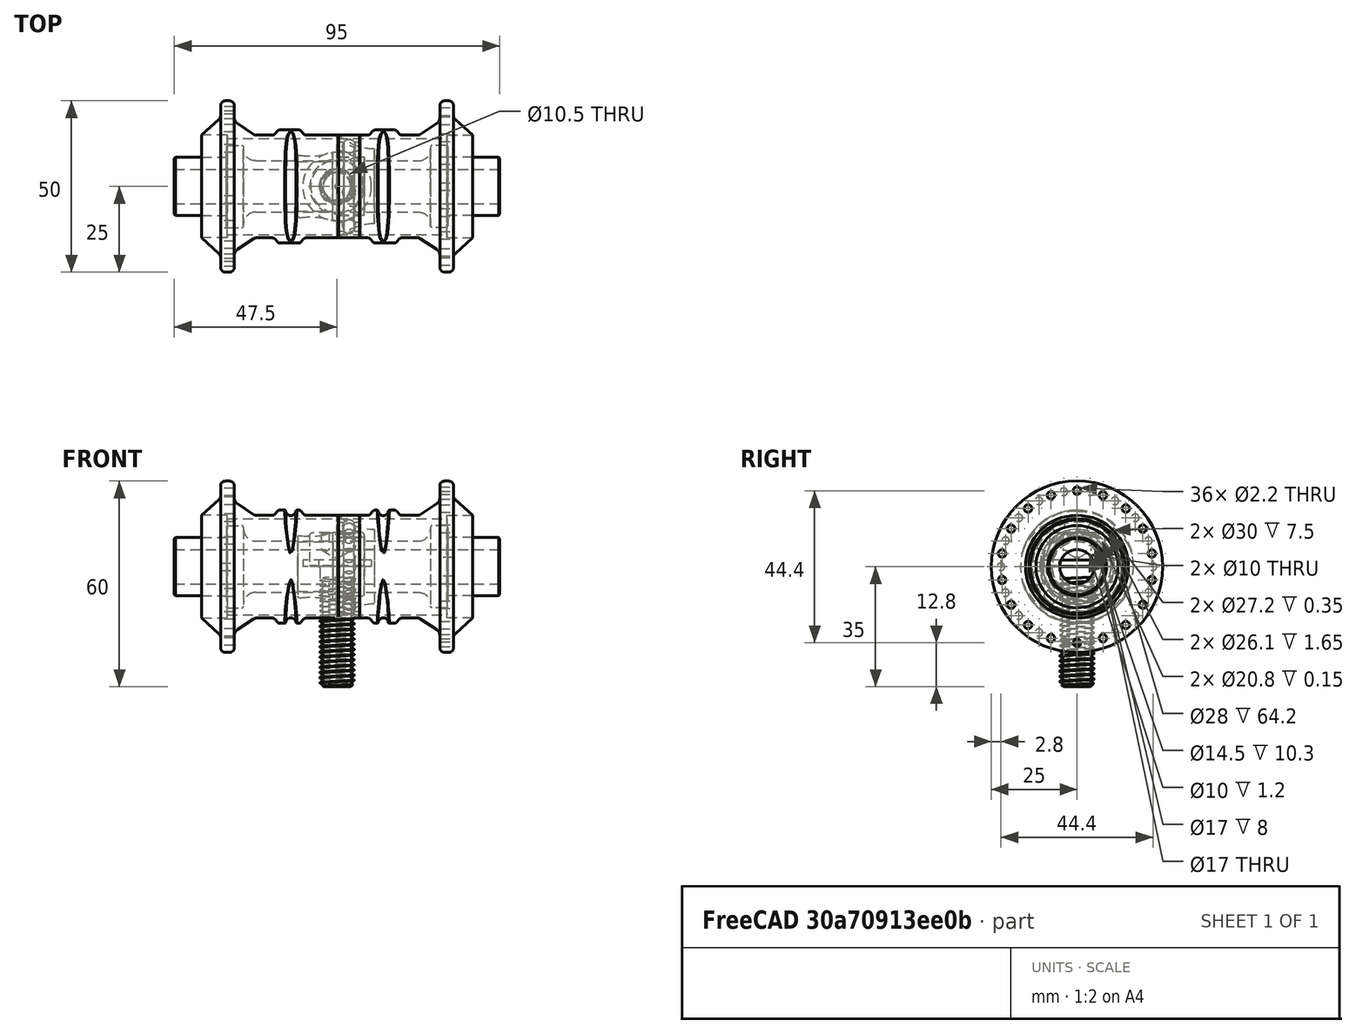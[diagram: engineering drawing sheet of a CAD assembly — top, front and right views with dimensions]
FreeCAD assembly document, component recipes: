
FREECAD ASSEMBLY — COMPONENT RECIPES ("Bike Hub")

This assembly document has 12 components, labeled P0..P11 below (a component is one placed body or linked part). 6 of them carry a construction recipe — the FreeCAD feature program that regenerates the part from scratch, quoted from this document or its linked companion documents; the rest are supplied as boundary geometry only. No exploded tour is included for this assembly.
COMPONENT P0 — recipe-attached ("Axle001", modeled in this document).
Construction recipe (the document's own serialized feature program — sketch geometry with constraints, then the solid features built on it; lengths are millimeters unless a unit is written):

FEATURE [Sketcher::SketchObject] Sketch
  ArcFitTolerance = 1e-06
  AttachmentSupport = -> [XZ_Plane]
  FullyConstrained = true
  MakeInternals = false
  MapMode = 5
  Placement = pos=(0,0,0) rot=(1,0,0;1.5708rad)
  sketch-geometry (19):
    g0: LineSegment StartX=0 StartY=0 StartZ=0 EndX=-47.5 EndY=0 EndZ=0
    g1: LineSegment StartX=-47.5 StartY=0 StartZ=0 EndX=-47.5 EndY=8.14645 EndZ=0
    g2: LineSegment StartX=-47.1464 StartY=8.5 StartZ=0 EndX=-32.8 EndY=8.5 EndZ=0
    g3: LineSegment StartX=-32.3 StartY=9 StartZ=0 EndX=-32.3 EndY=11.5 EndZ=0
    g4: LineSegment StartX=-31.8 StartY=12 StartZ=0 EndX=-27.8 EndY=12 EndZ=0
    g5: LineSegment StartX=-27.3 StartY=11.5 StartZ=0 EndX=-27.3 EndY=11 EndZ=0
    g6: LineSegment StartX=-23.8 StartY=7.5 StartZ=0 EndX=0 EndY=7.5 EndZ=0
    g7: LineSegment StartX=0 StartY=7.5 StartZ=0 EndX=0 EndY=0 EndZ=0
    g8: ArcOfCircle CenterX=-27.8 CenterY=11.5 CenterZ=0 NormalX=0 NormalY=0 NormalZ=1 AngleXU=0 Radius=0.5 StartAngle=0 EndAngle=1.5708
    g9: GeomPoint [constr] X=-27.3 Y=12 Z=0
    g10: ArcOfCircle CenterX=-23.8 CenterY=11 CenterZ=0 NormalX=0 NormalY=0 NormalZ=1 AngleXU=0 Radius=3.5 StartAngle=3.14159 EndAngle=4.71239
    g11: GeomPoint [constr] X=-27.3 Y=7.5 Z=0
    g12: ArcOfCircle CenterX=-31.8 CenterY=11.5 CenterZ=0 NormalX=0 NormalY=0 NormalZ=1 AngleXU=0 Radius=0.5 StartAngle=1.5708 EndAngle=3.14159
    g13: GeomPoint [constr] X=-32.3 Y=12 Z=0
    g14: ArcOfCircle CenterX=-32.8 CenterY=9 CenterZ=0 NormalX=0 NormalY=0 NormalZ=1 AngleXU=0 Radius=0.5 StartAngle=4.71239 EndAngle=6.28319
    g15: GeomPoint [constr] X=-32.3 Y=8.5 Z=0
    g16: ArcOfCircle [constr] CenterX=-47.1464 CenterY=8.14645 CenterZ=0 NormalX=0 NormalY=0 NormalZ=1 AngleXU=0 Radius=0.353553 StartAngle=1.5708 EndAngle=3.14159
    g17: GeomPoint [constr] X=-47.5 Y=8.5 Z=0
    g18: LineSegment StartX=-47.1464 StartY=8.5 StartZ=0 EndX=-47.5 EndY=8.14645 EndZ=0
  constraints (45):
    c: Coincident(g-1,g0)
    c: PointOnObject(g0,g-1)
    c: Coincident(g0,g1)
    c: Vertical(g1)
    c: Horizontal(g2)
    c: Horizontal(g4)
    c: Vertical(g5)
    c: Horizontal(g6)
    c: Coincident(g6,g7)
    c: Coincident(g7,g0)
    c: Vertical(g7)
    c: Vertical(g3)
    c: DistanceX(g0,g0) = 47.5
    c: DistanceY(g1,g17) = 8.5
    c: Distance(g13,g0) = 12
    c: DistanceX(g13,g-1) = 32.3
    c: DistanceX(g13,g9) = 5
    c: DistanceY(g7,g7) = 7.5
    c: PointOnObject(g9,g4)
    c: PointOnObject(g9,g5)
    c: Tangent(g4,g8) = 1.5708
    c: Tangent(g5,g8) = 1.5708
    c: PointOnObject(g11,g5)
    c: PointOnObject(g11,g6)
    c: Tangent(g5,g10) = -1.5708
    c: Tangent(g6,g10) = -1.5708
    c: PointOnObject(g13,g3)
    c: PointOnObject(g13,g4)
    c: Tangent(g3,g12) = 1.5708
    c: Tangent(g4,g12) = 1.5708
    c: PointOnObject(g15,g2)
    c: PointOnObject(g15,g3)
    c: Tangent(g2,g14) = -1.5708
    c: Tangent(g3,g14) = -1.5708
    c: Radius(g8) = 0.5
    c: Equal(g8,g12)
    c: Equal(g12,g14)
    c: Radius(g10) = 3.5
    c: PointOnObject(g17,g1)
    c: PointOnObject(g17,g2)
    c: Tangent(g1,g16) = 1.5708
    c: Tangent(g2,g16) = 1.5708
    c: Coincident(g18,g1)
    c: Coincident(g18,g2)
    c: Distance(g18,g18) = 0.5
FEATURE [PartDesign::Revolution] Revolution
  Angle = 360
  Angle2 = 60
  Axis = (1,0,0)
  Base = (0,0,0)
  Placement = pos=(0,0,0) rot=(1,0,0;1.5708rad)
  Profile = -> Sketch
  ReferenceAxis = -> X_Axis
  Refine = true
  Suppressed = false
  Type = 0
FEATURE [PartDesign::Hole] Hole
  BaseFeature = -> Revolution
  CustomThreadClearance = 0
  Depth = 117.922
  DepthType = 1
  Diameter = 10
  DrillForDepth = false
  DrillPoint = 1
  DrillPointAngle = 118
  HoleCutCountersinkAngle = 90
  HoleCutCustomValues = false
  HoleCutDepth = 0
  HoleCutDiameter = 6.1
  HoleCutType = 0
  ModelThread = false
  Placement = pos=(0,0,0) rot=(1,0,0;1.5708rad)
  Profile = -> Revolution [Face5]
  Refine = true
  Suppressed = false
  Tapered = false
  TaperedAngle = 90
  ThreadClass = 0
  ThreadDepth = 117.922
  ThreadDepthType = 0
  ThreadDirection = 0
  ThreadFit = 0
  ThreadSize = 0
  ThreadType = 0
  Threaded = false
  UseCustomThreadClearance = false
FEATURE [PartDesign::Mirrored] Mirrored
  BaseFeature = -> Hole
  MirrorPlane = -> YZ_Plane
  Originals = -> [Hole]
  Placement = pos=(0,0,0) rot=(1,0,0;1.5708rad)
  Refine = true
  Suppressed = false
  TransformMode = 1
FEATURE [PartDesign::Body] Body  label="Axle"
  AllowCompound = false
  Group = -> [Sketch,Revolution,Hole,Mirrored]
  Origin = -> Origin
  Tip = -> Mirrored
COMPONENT P1 — geometry summary ("Bearing001"; no construction recipe available for this part):
  bounding box: 30.0 x 30.0 x 7.0 mm
  tessellated surface: 109,814 triangles
  volume: 2172 mm^3 (34% of its bounding box)
  symmetry: mirror-symmetric across its x mid-plane
COMPONENT P2 — geometry summary ("Bearing002"; no construction recipe available for this part):
  bounding box: 30.0 x 30.0 x 7.0 mm
  tessellated surface: 109,814 triangles
  volume: 2172 mm^3 (34% of its bounding box)
  symmetry: mirror-symmetric across its x mid-plane
COMPONENT P3 — recipe-attached ("Bearing Cover001", modeled in this document).
Construction recipe (the document's own serialized feature program — sketch geometry with constraints, then the solid features built on it; lengths are millimeters unless a unit is written):

FEATURE [Sketcher::SketchObject] Sketch008
  ArcFitTolerance = 1e-06
  AttachmentSupport = -> [XZ_Plane002]
  FullyConstrained = true
  MakeInternals = false
  MapMode = 5
  Placement = pos=(0,0,0) rot=(1,0,0;1.5708rad)
  sketch-geometry (8):
    g0: LineSegment StartX=0 StartY=0 StartZ=0 EndX=10.9 EndY=0 EndZ=0
    g1: LineSegment StartX=0 StartY=0 StartZ=0 EndX=0 EndY=10.9 EndZ=0
    g2: LineSegment StartX=0 StartY=10.9 StartZ=0 EndX=0.3 EndY=10.9 EndZ=0
    g3: LineSegment StartX=0.3 StartY=10.9 StartZ=0 EndX=0.3 EndY=15 EndZ=0
    g4: LineSegment StartX=0.3 StartY=15 StartZ=0 EndX=0.5 EndY=15 EndZ=0
    g5: LineSegment StartX=10.9 StartY=0 StartZ=0 EndX=10.9 EndY=10.9 EndZ=0
    g6: ArcOfCircle CenterX=10.9 CenterY=26.1402 CenterZ=0 NormalX=0 NormalY=0 NormalZ=1 AngleXU=0 Radius=15.2402 StartAngle=3.96134 EndAngle=4.71239
    g7: LineSegment [constr] StartX=10.9 StartY=10.9 StartZ=0 EndX=20.01 EndY=10.9 EndZ=0
  constraints (24):
    c: Coincident(g-1,g0)
    c: PointOnObject(g0,g-1)
    c: Coincident(g0,g1)
    c: PointOnObject(g1,g-2)
    c: Coincident(g1,g2)
    c: Horizontal(g2)
    c: Coincident(g2,g3)
    c: DistanceX(g0,g0) = 10.9
    c: DistanceY(g1,g1) = 10.9
    c: Coincident(g4,g3)
    c: Vertical(g3)
    c: Horizontal(g4)
    c: DistanceX(g2,g2) = 0.3
    c: DistanceX(g4,g4) = 0.2
    c: DistanceY(g-1,g3) = 15
    c: Coincident(g0,g5)
    c: Vertical(g5)
    c: Coincident(g6,g5)
    c: Coincident(g6,g4)
    c: Coincident(g7,g5)
    c: Horizontal(g7)
    c: Tangent(g6,g7)
    c: Horizontal(g5,g2)
    c: DistanceX(g7,g7) = 9.11
FEATURE [PartDesign::Revolution] Revolution002
  Angle = 360
  Angle2 = 60
  Axis = (1,0,0)
  Base = (0,0,0)
  Placement = pos=(0,0,0) rot=(1,0,0;1.5708rad)
  Profile = -> Sketch008
  ReferenceAxis = -> X_Axis002
  Refine = true
  Suppressed = false
  Type = 0
FEATURE [Sketcher::SketchObject] Sketch009
  ArcFitTolerance = 1e-06
  AttachmentSupport = -> [Revolution002]
  FullyConstrained = true
  MakeInternals = false
  MapMode = 5
  Placement = pos=(0,0,0) rot=(0.707107,0,-0.707107;3.14159rad)
  sketch-geometry (1):
    g0: Circle CenterX=0 CenterY=0 CenterZ=0 NormalX=0 NormalY=0 NormalZ=1 AngleXU=0 Radius=8.5
  constraints (2):
    c: Coincident(g0,g-1)
    c: Diameter(g0) = 17
FEATURE [PartDesign::Pocket] Pocket004
  BaseFeature = -> Revolution002
  Direction = (1,0,2e-16)
  Length = 8
  Length2 = 5
  Placement = pos=(0,0,0) rot=(1,0,0;1.5708rad)
  Profile = -> Sketch009
  ReferenceAxis = -> Sketch009 [N_Axis]
  Refine = true
  Suppressed = false
  Type = 0
FEATURE [Sketcher::SketchObject] Sketch010
  ArcFitTolerance = 1e-06
  AttachmentSupport = -> [Pocket004]
  FullyConstrained = true
  MakeInternals = false
  MapMode = 5
  Placement = pos=(10.9,0,0) rot=(0.707107,0,0.707107;3.14159rad)
  sketch-geometry (1):
    g0: Circle CenterX=0 CenterY=0 CenterZ=0 NormalX=0 NormalY=0 NormalZ=1 AngleXU=0 Radius=5
  constraints (2):
    c: Coincident(g0,g-1)
    c: Diameter(g0) = 10
FEATURE [PartDesign::Pocket] Pocket005
  BaseFeature = -> Pocket004
  Direction = (-1,0,2e-16)
  Length = 5
  Length2 = 5
  Placement = pos=(0,0,0) rot=(1,0,0;1.5708rad)
  Profile = -> Sketch010
  ReferenceAxis = -> Sketch010 [N_Axis]
  Refine = true
  Suppressed = false
  Type = 1
FEATURE [PartDesign::Body] Body002  label="Bearing Cover"
  AllowCompound = false
  Group = -> [Sketch008,Revolution002,Sketch009,Pocket004,Sketch010,Pocket005]
  Origin = -> Origin002
  Tip = -> Pocket005
COMPONENT P4 — same part as P3; its construction recipe is shown at P3.
COMPONENT P5 — recipe-attached ("Bolt Cover001", modeled in this document).
Construction recipe (the document's own serialized feature program — sketch geometry with constraints, then the solid features built on it; lengths are millimeters unless a unit is written):

FEATURE [Sketcher::SketchObject] Sketch011
  ArcFitTolerance = 1e-06
  AttachmentSupport = -> [XZ_Plane004]
  FullyConstrained = true
  MakeInternals = false
  MapMode = 5
  Placement = pos=(0,0,0) rot=(1,0,0;1.5708rad)
  sketch-geometry (5):
    g0: LineSegment StartX=0 StartY=0 StartZ=0 EndX=-11.5 EndY=0 EndZ=0
    g1: LineSegment StartX=-11.5 StartY=0 StartZ=0 EndX=-11.5 EndY=9.2 EndZ=0
    g2: LineSegment StartX=0 StartY=0 StartZ=0 EndX=0 EndY=10 EndZ=0
    g3: LineSegment StartX=0 StartY=10 StartZ=0 EndX=-1.3 EndY=10 EndZ=0
    g4: ArcOfCircle CenterX=-7.9118 CenterY=28.8755 CenterZ=0 NormalX=0 NormalY=0 NormalZ=1 AngleXU=0 Radius=20 StartAngle=4.532 EndAngle=5.04932
  constraints (15):
    c: Coincident(g-1,g0)
    c: PointOnObject(g0,g-1)
    c: Coincident(g0,g1)
    c: Vertical(g1)
    c: Coincident(g0,g2)
    c: PointOnObject(g2,g-2)
    c: Coincident(g2,g3)
    c: Horizontal(g3)
    c: Coincident(g4,g3)
    c: Coincident(g4,g1)
    c: DistanceX(g0,g0) = 11.5
    c: DistanceY(g1,g1) = 9.2
    c: DistanceY(g2,g2) = 10
    c: DistanceX(g3,g3) = 1.3
    c: Radius(g4) = 20
FEATURE [PartDesign::Revolution] Revolution003
  Angle = 360
  Angle2 = 60
  Axis = (1,0,0)
  Base = (0,0,0)
  Placement = pos=(0,0,0) rot=(1,0,0;1.5708rad)
  Profile = -> Sketch011
  ReferenceAxis = -> X_Axis004
  Refine = true
  Suppressed = false
  Type = 0
FEATURE [Sketcher::SketchObject] Sketch012
  ArcFitTolerance = 1e-06
  AttachmentSupport = -> [Revolution003]
  FullyConstrained = true
  MakeInternals = false
  MapMode = 5
  Placement = pos=(-11.5,0,0) rot=(0.707107,0,-0.707107;3.14159rad)
  sketch-geometry (1):
    g0: Circle CenterX=0 CenterY=0 CenterZ=0 NormalX=0 NormalY=0 NormalZ=1 AngleXU=0 Radius=5
  constraints (2):
    c: Diameter(g0) = 10
    c: Coincident(g0,g-1)
FEATURE [PartDesign::Hole] Hole001
  BaseFeature = -> Revolution003
  CustomThreadClearance = 0
  Depth = 61.6685
  DepthType = 1
  Diameter = 10
  DrillForDepth = false
  DrillPoint = 1
  DrillPointAngle = 118
  HoleCutCountersinkAngle = 90
  HoleCutCustomValues = false
  HoleCutDepth = 10.3
  HoleCutDiameter = 14.5
  HoleCutType = 1
  ModelThread = false
  Placement = pos=(0,0,0) rot=(1,0,0;1.5708rad)
  Profile = -> Sketch012
  Refine = true
  Suppressed = false
  Tapered = false
  TaperedAngle = 90
  ThreadClass = 0
  ThreadDepth = 61.6685
  ThreadDepthType = 0
  ThreadDirection = 0
  ThreadFit = 0
  ThreadSize = 0
  ThreadType = 0
  Threaded = false
  UseCustomThreadClearance = false
FEATURE [PartDesign::Fillet] Fillet001
  Base = -> Hole001 [Edge1]
  BaseFeature = -> Hole001
  Placement = pos=(0,0,0) rot=(1,0,0;1.5708rad)
  Radius = 0.5
  Refine = true
  SupportTransform = false
  Suppressed = false
  UseAllEdges = false
FEATURE [PartDesign::Body] Body003  label="Bolt Cover"
  AllowCompound = false
  Group = -> [Sketch011,Revolution003,Sketch012,Hole001,Fillet001]
  Origin = -> Origin004
  Tip = -> Fillet001
COMPONENT P6 — same part as P5; its construction recipe is shown at P5.
COMPONENT P7 — recipe-attached ("Hub Cage001", modeled in this document).
Construction recipe (the document's own serialized feature program — sketch geometry with constraints, then the solid features built on it; lengths are millimeters unless a unit is written):

FEATURE [Sketcher::SketchObject] Sketch001
  ArcFitTolerance = 1e-06
  AttachmentSupport = -> [XZ_Plane001]
  FullyConstrained = true
  MakeInternals = false
  MapMode = 5
  Placement = pos=(0,0,0) rot=(1,0,0;1.5708rad)
  sketch-geometry (31):
    g0: LineSegment StartX=0 StartY=0 StartZ=0 EndX=-39.6 EndY=0 EndZ=0
    g1: LineSegment StartX=-39.6 StartY=0 StartZ=0 EndX=-39.6 EndY=15 EndZ=0
    g2: LineSegment StartX=-39.6 StartY=15 StartZ=0 EndX=-34.4676 EndY=19.5825 EndZ=0
    g3: LineSegment StartX=-34 StartY=20.6268 StartZ=0 EndX=-34 EndY=23.6 EndZ=0
    g4: LineSegment StartX=-32.6 StartY=25 StartZ=0 EndX=-31.4 EndY=25 EndZ=0
    g5: LineSegment StartX=-30 StartY=23.6 StartZ=0 EndX=-30 EndY=20.0704 EndZ=0
    g6: LineSegment StartX=-29.1094 StartY=18.4063 StartZ=0 EndX=-24.2519 EndY=15.1679 EndZ=0
    g7: LineSegment StartX=-23.6972 StartY=15 StartZ=0 EndX=-18.8806 EndY=15 EndZ=0
    g8: LineSegment StartX=-18.0998 StartY=15.3753 StartZ=0 EndX=-17.5002 EndY=16.1247 EndZ=0
    g9: LineSegment StartX=-16.7194 StartY=16.5 StartZ=0 EndX=-11.1806 EndY=16.5 EndZ=0
    g10: LineSegment StartX=-10.3998 StartY=16.1247 StartZ=0 EndX=-9.80024 EndY=15.3753 EndZ=0
    g11: LineSegment StartX=-9.01938 StartY=15 StartZ=0 EndX=0 EndY=15 EndZ=0
    g12: LineSegment StartX=0 StartY=15 StartZ=0 EndX=0 EndY=0 EndZ=0
    g13: ArcOfCircle CenterX=-32.6 CenterY=23.6 CenterZ=0 NormalX=0 NormalY=0 NormalZ=1 AngleXU=0 Radius=1.4 StartAngle=1.5708 EndAngle=3.14159
    g14: GeomPoint [constr] X=-34 Y=25 Z=0
    g15: ArcOfCircle CenterX=-31.4 CenterY=23.6 CenterZ=0 NormalX=0 NormalY=0 NormalZ=1 AngleXU=0 Radius=1.4 StartAngle=0 EndAngle=1.5708
    g16: GeomPoint [constr] X=-30 Y=25 Z=0
    g17: ArcOfCircle CenterX=-35.4 CenterY=20.6268 CenterZ=0 NormalX=0 NormalY=0 NormalZ=1 AngleXU=0 Radius=1.4 StartAngle=5.44124 EndAngle=6.28319
    g18: GeomPoint [constr] X=-34 Y=20 Z=0
    g19: ArcOfCircle CenterX=-28 CenterY=20.0704 CenterZ=0 NormalX=0 NormalY=0 NormalZ=1 AngleXU=0 Radius=2 StartAngle=3.14159 EndAngle=4.12439
    g20: GeomPoint [constr] X=-30 Y=19 Z=0
    g21: ArcOfCircle CenterX=-23.6972 CenterY=16 CenterZ=0 NormalX=0 NormalY=0 NormalZ=1 AngleXU=0 Radius=1 StartAngle=4.12439 EndAngle=4.71239
    g22: GeomPoint [constr] X=-24 Y=15 Z=0
    g23: ArcOfCircle CenterX=-18.8806 CenterY=16 CenterZ=0 NormalX=0 NormalY=0 NormalZ=1 AngleXU=0 Radius=1 StartAngle=4.71239 EndAngle=5.60844
    g24: GeomPoint [constr] X=-18.4 Y=15 Z=0
    g25: ArcOfCircle CenterX=-16.7194 CenterY=15.5 CenterZ=0 NormalX=0 NormalY=0 NormalZ=1 AngleXU=0 Radius=1 StartAngle=1.5708 EndAngle=2.46685
    g26: GeomPoint [constr] X=-17.2 Y=16.5 Z=0
    g27: ArcOfCircle CenterX=-11.1806 CenterY=15.5 CenterZ=0 NormalX=0 NormalY=0 NormalZ=1 AngleXU=0 Radius=1 StartAngle=0.674741 EndAngle=1.5708
    g28: GeomPoint [constr] X=-10.7 Y=16.5 Z=0
    g29: ArcOfCircle CenterX=-9.01938 CenterY=16 CenterZ=0 NormalX=0 NormalY=0 NormalZ=1 AngleXU=0 Radius=1 StartAngle=3.81633 EndAngle=4.71239
    g30: GeomPoint [constr] X=-9.5 Y=15 Z=0
  constraints (74):
    c: Coincident(g-1,g0)
    c: PointOnObject(g0,g-1)
    c: Coincident(g0,g1)
    c: Vertical(g1)
    c: Coincident(g1,g2)
    c: Vertical(g3)
    c: Horizontal(g4)
    c: Vertical(g5)
    c: Horizontal(g7)
    c: Horizontal(g9)
    c: Horizontal(g11)
    c: Coincident(g11,g12)
    c: Coincident(g12,g0)
    c: Vertical(g12)
    c: DistanceX(g0,g0) = 39.6
    c: Distance(g0,g4) = 25
    c: DistanceY(g-1,g1) = 15
    c: DistanceY(g-1,g18) = 20
    c: DistanceY(g-1,g20) = 19
    c: DistanceX(g14,g16) = 4
    c: DistanceX(g14,g-1) = 34
    c: DistanceX(g22,g-1) = 24
    c: DistanceX(g26,g28) = 6.5
    c: DistanceX(g30,g11) = 9.5
    c: DistanceX(g28,g-1) = 10.7
    c: DistanceY(g-1,g28) = 16.5
    c: PointOnObject(g14,g3)
    c: PointOnObject(g14,g4)
    c: Tangent(g3,g13) = 1.5708
    c: Tangent(g4,g13) = 1.5708
    c: PointOnObject(g16,g4)
    c: PointOnObject(g16,g5)
    c: Tangent(g4,g15) = 1.5708
    c: Tangent(g5,g15) = 1.5708
    c: PointOnObject(g18,g2)
    c: PointOnObject(g18,g3)
    c: Tangent(g2,g17) = -1.5708
    c: Tangent(g3,g17) = -1.5708
    c: PointOnObject(g20,g5)
    c: PointOnObject(g20,g6)
    c: Tangent(g5,g19) = -1.5708
    c: Tangent(g6,g19) = -1.5708
    c: Equal(g17,g13)
    c: Equal(g13,g15)
    c: Radius(g13) = 1.4
    c: Radius(g19) = 2
    c: PointOnObject(g22,g6)
    c: PointOnObject(g22,g7)
    c: Tangent(g6,g21) = -1.5708
    c: Tangent(g7,g21) = -1.5708
    c: PointOnObject(g24,g7)
    c: PointOnObject(g24,g8)
    c: Tangent(g7,g23) = -1.5708
    c: Tangent(g8,g23) = -1.5708
    c: PointOnObject(g26,g8)
    c: PointOnObject(g26,g9)
    c: Tangent(g8,g25) = 1.5708
    c: Tangent(g9,g25) = 1.5708
    c: PointOnObject(g28,g9)
    c: PointOnObject(g28,g10)
    c: Tangent(g9,g27) = 1.5708
    c: Tangent(g10,g27) = 1.5708
    c: PointOnObject(g30,g10)
    c: PointOnObject(g30,g11)
    c: Tangent(g10,g29) = -1.5708
    c: Tangent(g11,g29) = -1.5708
    c: Radius(g21) = 1
    c: Horizontal(g11,g22)
    c: Equal(g21,g23)
    c: Equal(g23,g25)
    c: Equal(g25,g27)
    c: Equal(g27,g29)
    c: Horizontal(g11,g1)
    c: Equal(g8,g10)
FEATURE [PartDesign::Revolution] Revolution001
  Angle = 360
  Angle2 = 60
  Axis = (1,0,0)
  Base = (0,0,0)
  Placement = pos=(0,0,0) rot=(1,0,0;1.5708rad)
  Profile = -> Sketch001
  ReferenceAxis = -> X_Axis001
  Refine = true
  Suppressed = false
  Type = 0
FEATURE [Sketcher::SketchObject] Sketch002
  ArcFitTolerance = 1e-06
  AttachmentSupport = -> [Revolution001]
  FullyConstrained = true
  MakeInternals = false
  MapMode = 5
  Placement = pos=(-39.6,0,0) rot=(0.707107,0,-0.707107;3.14159rad)
  sketch-geometry (1):
    g0: Circle CenterX=0 CenterY=0 CenterZ=0 NormalX=0 NormalY=0 NormalZ=1 AngleXU=0 Radius=15
  constraints (2):
    c: Diameter(g0) = 30
    c: Coincident(g0,g-1)
FEATURE [PartDesign::Pocket] Pocket
  BaseFeature = -> Revolution001
  Direction = (1,0,2e-16)
  Length = 7.5
  Length2 = 5
  Placement = pos=(0,0,0) rot=(1,0,0;1.5708rad)
  Profile = -> Sketch002
  ReferenceAxis = -> Sketch002 [N_Axis]
  Refine = true
  Suppressed = false
  Type = 0
FEATURE [Sketcher::SketchObject] Sketch003
  ArcFitTolerance = 1e-06
  AttachmentSupport = -> [Pocket]
  FullyConstrained = true
  MakeInternals = false
  MapMode = 5
  Placement = pos=(0,0,0) rot=(0.707107,0,0.707107;3.14159rad)
  sketch-geometry (1):
    g0: Circle CenterX=0 CenterY=0 CenterZ=0 NormalX=0 NormalY=0 NormalZ=1 AngleXU=0 Radius=14
  constraints (2):
    c: Diameter(g0) = 28
    c: Coincident(g0,g-1)
FEATURE [PartDesign::Pocket] Pocket001
  BaseFeature = -> Pocket
  Direction = (-1,0,2e-16)
  Length = 5
  Length2 = 5
  Placement = pos=(0,0,0) rot=(1,0,0;1.5708rad)
  Profile = -> Sketch003
  ReferenceAxis = -> Sketch003 [N_Axis]
  Refine = true
  Suppressed = false
  Type = 1
FEATURE [PartDesign::Plane] DatumPlane
  AttachmentOffset = pos=(0,0,-13.5) rot=(0,0,1;0rad)
  AttachmentSupport = -> [Pocket001]
  Length = 60
  MapMode = 5
  Placement = pos=(-13.5,0,3e-15) rot=(0.707107,0,0.707107;3.14159rad)
  ResizeMode = 0
  Width = 60
FEATURE [Sketcher::SketchObject] Sketch004
  ArcFitTolerance = 1e-06
  AttachmentSupport = -> [DatumPlane]
  FullyConstrained = true
  MakeInternals = false
  MapMode = 5
  Placement = pos=(-13.5,0,3e-15) rot=(0.707107,0,0.707107;3.14159rad)
  sketch-geometry (5):
    g0: Ellipse CenterX=0 CenterY=0 CenterZ=0 NormalX=0 NormalY=0 NormalZ=1 MajorRadius=18.1 MinorRadius=16.4 AngleXU=-1.5708
    g1: LineSegment [constr] StartX=6.27002e-06 StartY=-18.1 StartZ=0 EndX=-6.27002e-06 EndY=18.1 EndZ=0
    g2: LineSegment [constr] StartX=16.4 StartY=5.68113e-06 StartZ=0 EndX=-16.4 EndY=-5.68113e-06 EndZ=0
    g3: GeomPoint [constr] X=2.65292e-06 Y=-7.65833 Z=0
    g4: GeomPoint [constr] X=-2.65292e-06 Y=7.65833 Z=0
  constraints (5):
    c: InternalAlignment(g1-g4 -> g0) x4
    c: Distance(g0,g2) = 16.4
    c: Angle(g2) = 3.14159
    c: Distance(g0,g1) = 18.1
    c: Coincident(g0,g-1)
FEATURE [Sketcher::SketchObject] Sketch005
  ArcFitTolerance = 1e-06
  AttachmentSupport = -> [XY_Plane001]
  ExternalGeometry = -> [Sketch004]
  FullyConstrained = true
  MakeInternals = false
  MapMode = 5
  sketch-geometry (1):
    g0: Circle CenterX=-13.5 CenterY=18.1 CenterZ=0 NormalX=0 NormalY=0 NormalZ=1 AngleXU=0 Radius=1.5
  constraints (2):
    c: Diameter(g0) = 3
    c: Coincident(g0,g-3)
FEATURE [PartDesign::SubtractivePipe] SubtractivePipe
  AuxilleryCurvelinear = true
  AuxillerySpineTangent = false
  BaseFeature = -> Pocket001
  Binormal = (0,0,0)
  Mode = 0
  Placement = pos=(0,0,0) rot=(1,0,0;1.5708rad)
  Profile = -> Sketch005
  Refine = true
  Spine = -> Sketch004
  SpineTangent = false
  Suppressed = false
  Transformation = 0
  Transition = 0
FEATURE [PartDesign::Mirrored] Mirrored001
  BaseFeature = -> SubtractivePipe
  MirrorPlane = -> Sketch005 [V_Axis]
  Originals = -> [SubtractivePipe]
  Placement = pos=(0,0,0) rot=(1,0,0;1.5708rad)
  Refine = true
  Suppressed = false
  TransformMode = 1
FEATURE [Sketcher::SketchObject] Sketch006
  ArcFitTolerance = 1e-06
  AttachmentSupport = -> [Mirrored001]
  FullyConstrained = true
  MakeInternals = false
  MapMode = 5
  Placement = pos=(-34,0,0) rot=(0.707107,0,-0.707107;3.14159rad)
  sketch-geometry (1):
    g0: Circle CenterX=0 CenterY=22.2 CenterZ=0 NormalX=0 NormalY=0 NormalZ=1 AngleXU=0 Radius=1.1
  constraints (3):
    c: Diameter(g0) = 2.2
    c: PointOnObject(g0,g-2)
    c: DistanceY(g-1,g0) = 22.2
FEATURE [PartDesign::Pocket] Pocket002
  BaseFeature = -> Mirrored001
  Direction = (1,0,2e-16)
  Length = 0
  Length2 = 5
  Placement = pos=(0,0,0) rot=(1,0,0;1.5708rad)
  Profile = -> Sketch006
  ReferenceAxis = -> Sketch006 [N_Axis]
  Refine = true
  Suppressed = false
  Type = 3
  UpToFace = -> Mirrored001 [Face14]
FEATURE [PartDesign::PolarPattern] PolarPattern
  Angle = 360
  Axis = -> Sketch006 [N_Axis]
  BaseFeature = -> Pocket002
  Mode = 0
  Occurrences = 18
  Offset = 120
  Originals = -> [Pocket002]
  Placement = pos=(0,0,0) rot=(1,0,0;1.5708rad)
  Refine = true
  Suppressed = false
  TransformMode = 0
FEATURE [Sketcher::SketchObject] Sketch007
  ArcFitTolerance = 1e-06
  AttachmentSupport = -> [PolarPattern]
  FullyConstrained = true
  MakeInternals = false
  MapMode = 5
  Placement = pos=(34,0,0) rot=(0.707107,0,0.707107;3.14159rad)
  sketch-geometry (2):
    g0: Circle CenterX=-3.85499 CenterY=21.8627 CenterZ=0 NormalX=0 NormalY=0 NormalZ=1 AngleXU=0 Radius=1.1
    g1: LineSegment [constr] StartX=-3.85499 StartY=21.8627 StartZ=0 EndX=4e-16 EndY=0 EndZ=0
  constraints (5):
    c: Diameter(g0) = 2.2
    c: Coincident(g1,g0)
    c: Coincident(g1,g-1)
    c: Distance(g1,g1) = 22.2
    c: Angle(g-2,g1) = 0.174533
FEATURE [PartDesign::Pocket] Pocket003
  BaseFeature = -> PolarPattern
  Direction = (-1,0,2e-16)
  Length = 0
  Length2 = 5
  Placement = pos=(0,0,0) rot=(1,0,0;1.5708rad)
  Profile = -> Sketch007
  ReferenceAxis = -> Sketch007 [N_Axis]
  Refine = true
  Suppressed = false
  Type = 3
  UpToFace = -> PolarPattern [Face53]
FEATURE [PartDesign::PolarPattern] PolarPattern001
  Angle = 360
  Axis = -> Sketch007 [N_Axis]
  BaseFeature = -> Pocket003
  Mode = 0
  Occurrences = 18
  Offset = 120
  Originals = -> [Pocket003]
  Placement = pos=(0,0,0) rot=(1,0,0;1.5708rad)
  Refine = true
  Suppressed = false
  TransformMode = 0
FEATURE [PartDesign::Fillet] Fillet
  Base = -> PolarPattern001 [Edge9,Edge15,Edge41,Edge35]
  BaseFeature = -> PolarPattern001
  Placement = pos=(0,0,0) rot=(1,0,0;1.5708rad)
  Radius = 0.3
  Refine = true
  SupportTransform = false
  Suppressed = false
  UseAllEdges = false
FEATURE [PartDesign::Body] Body001  label="Hub Cage"
  AllowCompound = false
  Group = -> [Sketch001,Revolution001,Sketch002,Pocket,Sketch003,Pocket001,DatumPlane,Sketch004,Sketch005,SubtractivePipe,Mirrored001,Sketch006,Pocket002,PolarPattern,Sketch007,Pocket003,PolarPattern001,Fillet]
  Origin = -> Origin001
  Tip = -> Fillet
COMPONENT P8 — geometry summary ("M10-Washer001"; no construction recipe available for this part):
  bounding box: 20.0 x 20.0 x 2.0 mm
  tessellated surface: 1,008 triangles
  volume: 455 mm^3 (57% of its bounding box)
  symmetry: revolution-symmetric about the x axis through its bounding-box center; 2-fold rotationally symmetric about the y axis; 2-fold rotationally symmetric about the z axis; mirror-symmetric across its x mid-plane, y mid-plane, z mid-plane
COMPONENT P9 — geometry summary ("M10-Washer002"; no construction recipe available for this part):
  bounding box: 20.0 x 20.0 x 2.0 mm
  tessellated surface: 1,008 triangles
  volume: 455 mm^3 (57% of its bounding box)
  symmetry: revolution-symmetric about the x axis through its bounding-box center; 2-fold rotationally symmetric about the y axis; 2-fold rotationally symmetric about the z axis; mirror-symmetric across its x mid-plane, y mid-plane, z mid-plane
COMPONENT P10 — geometry summary ("M10x35-Screw001"; no construction recipe available for this part):
  bounding box: 45.0 x 16.0 x 16.0 mm
  tessellated surface: 70,550 triangles
  volume: 3961 mm^3 (34% of its bounding box)
  symmetry: 6-fold rotationally symmetric about the x axis
COMPONENT P11 — geometry summary ("M10x35-Screw002"; no construction recipe available for this part):
  bounding box: 45.0 x 16.0 x 16.0 mm
  tessellated surface: 70,550 triangles
  volume: 3961 mm^3 (34% of its bounding box)
  symmetry: 6-fold rotationally symmetric about the x axis
PROVENANCE & LICENSES
A FreeCAD (.FCStd) document from a public repository crawl; recipes are the document's own serialized feature recipes (and, for linked parts, companion documents' recipes).
License: as declared in the source repository (recorded in the dataset sidecar).
